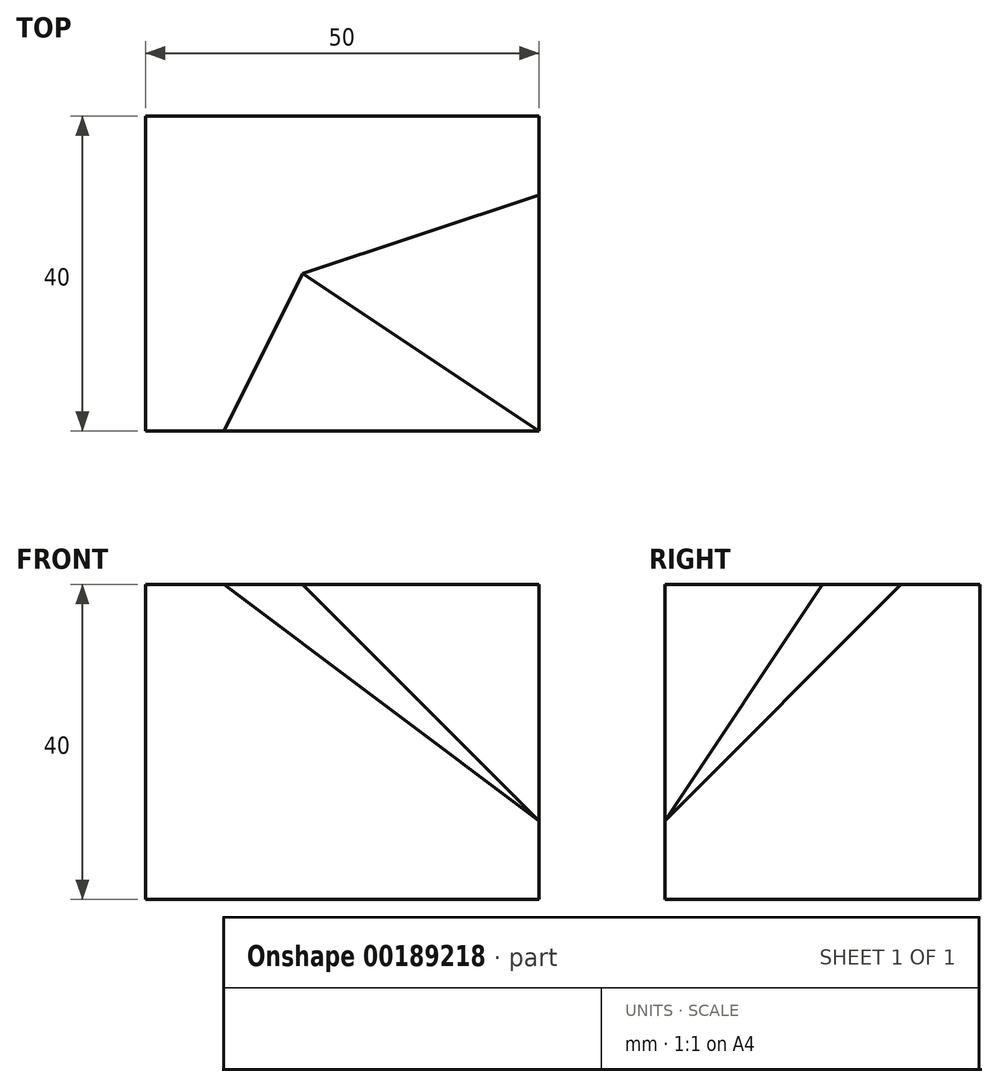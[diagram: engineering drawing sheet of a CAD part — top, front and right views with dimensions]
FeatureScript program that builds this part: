
annotation { "Feature Type Name" : "Feature", "Feature Type Description" : "" }
export const myFeature = defineFeature(function(context is Context, id is Id, definition is map)
    precondition{}
    {
        {
            var Q0;
            Q0=qCreatedBy(makeId("Top.planeOp"),FACE);
            var sketch = newSketch(context, id + "F0", { "sketchPlane" : qUnion([Q0])});
            skLineSegment(sketch, "E0.bottom", {"start": v(0, 0) * mm, "end": v(50, 0) * mm});
            skLineSegment(sketch, "E0.top", {"start": v(0, 40) * mm, "end": v(50, 40) * mm});
            skLineSegment(sketch, "E0.left", {"start": v(0, 0) * mm, "end": v(0, 40) * mm});
            skLineSegment(sketch, "E0.right", {"start": v(50, 0) * mm, "end": v(50, 40) * mm});
            skSolve(sketch);
        }
        {
            var Q0;
            Q0=makeQuery(id+"F0.imprint","IMPRINT",FACE,{"disambiguationData":[TD([[makeQuery(id+"F0.imprint","IMPRINT",EDGE,{"derivedFrom":sQuery(id+"F0.wireOp",EDGE,"E0.bottom")}),1.0]])]});
            extrude(context, id + "F1", {"entities" : qUnion([Q0]), "depth" : 40 * mm});
        }
        {
            var Q0;
            Q0=makeQuery(id+"F1.opExtrude","CAP_FACE",FACE,{"disambiguationData":[OSD([sQuery(id+"F0.wireOp",EDGE,"E0.bottom"),sQuery(id+"F0.wireOp",EDGE,"E0.top"),sQuery(id+"F0.wireOp",EDGE,"E0.left"),sQuery(id+"F0.wireOp",EDGE,"E0.right")])],"isStart":false});
            var sketch = newSketch(context, id + "F2", { "sketchPlane" : qUnion([Q0])});
            skPoint(sketch, "E1", {"position": v(10, 0) * mm});
            skPoint(sketch, "E2", {"position": v(20, 20) * mm});
            skPoint(sketch, "E3", {"position": v(50, 30) * mm});
            skSolve(sketch);
        }
        {
            var Q0;
            Q0=makeQuery(id+"F1.opExtrude","SWEPT_FACE",FACE,{"disambiguationData":[OSD([sQuery(id+"F0.wireOp",EDGE,"E0.bottom")])]});
            var sketch = newSketch(context, id + "F3", { "sketchPlane" : qUnion([Q0])});
            skPoint(sketch, "E4", {"position": v(50, 10) * mm});
            skSolve(sketch);
        }
        {
            var Q0;
            Q0=sQuery(id+"F2.wireOp",VERTEX,"E1");
            var Q1;
            Q1=sQuery(id+"F2.wireOp",VERTEX,"E2");
            var Q2;
            Q2=sQuery(id+"F3.wireOp",VERTEX,"E4");
            cPlane(context, id + "F4", {"entities" : qUnion([Q0, Q1, Q2]), "cplaneType" : CPlaneType.THREE_POINT, "offset" : 25 * mm, "width" : 150 * mm, "height" : 150 * mm});
        }
        {
            var Q0;
            Q0=qCreatedBy(id+"F4.planeOp",FACE);
            var sketch = newSketch(context, id + "F5", { "sketchPlane" : qUnion([Q0])});
            skLineSegment(sketch, "E5", {"start": v(-13.34, 14.04) * mm, "end": v(-1.12, 32.77) * mm});
            skLineSegment(sketch, "E6", {"start": v(-1.12, 32.77) * mm, "end": v(35.54, 3.51) * mm});
            skLineSegment(sketch, "E7", {"start": v(35.54, 3.51) * mm, "end": v(-13.34, 14.04) * mm});
            skSolve(sketch);
        }
        {
            var Q0;
            Q0 = qSketchRegion(id + "F5", true);
            extrude(context, id + "F6", {"entities" : qUnion([Q0]), "operationType" : NewBodyOperationType.REMOVE, "endBound" : BoundingType.THROUGH_ALL, "depth" : 25 * mm});
        }
        {
            var Q0;
            Q0=sQuery(id+"F2.wireOp",VERTEX,"E2");
            var Q1;
            Q1=sQuery(id+"F2.wireOp",VERTEX,"E3");
            var Q2;
            Q2=sQuery(id+"F3.wireOp",VERTEX,"E4");
            cPlane(context, id + "F7", {"entities" : qUnion([Q0, Q1, Q2]), "cplaneType" : CPlaneType.THREE_POINT, "offset" : 25 * mm, "width" : 150 * mm, "height" : 150 * mm});
        }
        {
            var Q0;
            Q0=qCreatedBy(id+"F7.planeOp",FACE);
            var sketch = newSketch(context, id + "F8", { "sketchPlane" : qUnion([Q0])});
            skLineSegment(sketch, "E8", {"start": v(16.22, 42.43) * mm, "end": v(47.04, 49.5) * mm});
            skLineSegment(sketch, "E9", {"start": v(47.04, 49.5) * mm, "end": v(47.04, 7.07) * mm});
            skLineSegment(sketch, "E10", {"start": v(47.04, 7.07) * mm, "end": v(16.22, 42.43) * mm});
            skSolve(sketch);
        }
        {
            var Q0;
            Q0 = qSketchRegion(id + "F8", true);
            extrude(context, id + "F9", {"entities" : qUnion([Q0]), "operationType" : NewBodyOperationType.REMOVE, "endBound" : BoundingType.THROUGH_ALL, "depth" : 25 * mm});
        }
    });
